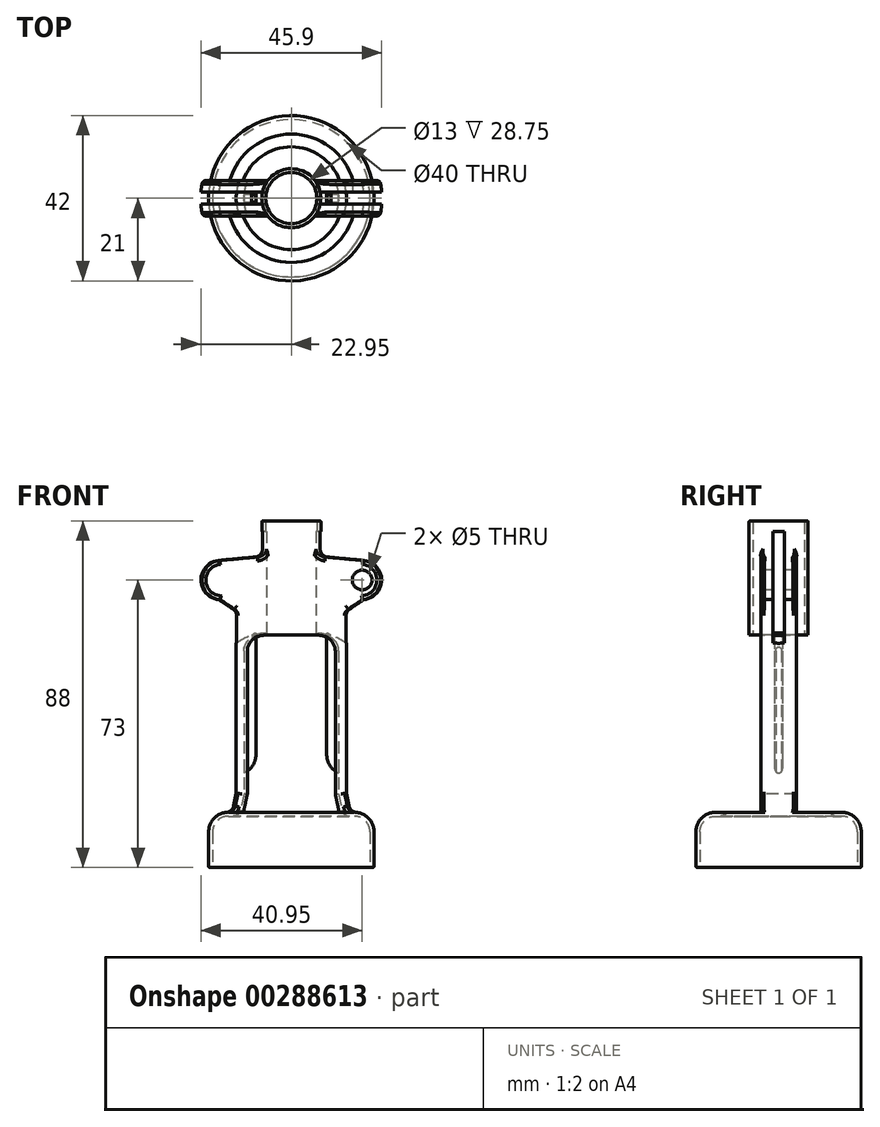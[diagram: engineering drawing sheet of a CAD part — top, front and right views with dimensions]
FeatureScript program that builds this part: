
annotation { "Feature Type Name" : "Feature", "Feature Type Description" : "" }
export const myFeature = defineFeature(function(context is Context, id is Id, definition is map)
    precondition{}
    {
        {
            var Q0;
            Q0=qCreatedBy(makeId("Front.planeOp"),FACE);
            var sketch = newSketch(context, id + "F0", { "sketchPlane" : qUnion([Q0])});
            skLineSegment(sketch, "E0", {"start": v(0, 0) * mm, "end": v(0, 88) * mm, "construction": true});
            skLineSegment(sketch, "E1", {"start": v(0, 88) * mm, "end": v(7.5, 88) * mm, "construction": true});
            skLineSegment(sketch, "E2", {"start": v(0, 79) * mm, "end": v(7.5, 79) * mm, "construction": true});
            skLineSegment(sketch, "E3", {"start": v(0, 73) * mm, "end": v(23, 73) * mm, "construction": true});
            skLineSegment(sketch, "E4", {"start": v(0, 65) * mm, "end": v(14, 65) * mm, "construction": true});
            skLineSegment(sketch, "E5", {"start": v(0, 0) * mm, "end": v(21, 0) * mm, "construction": true});
            skLineSegment(sketch, "E6", {"start": v(21, 0) * mm, "end": v(21, 14) * mm, "construction": true});
            skLineSegment(sketch, "E7", {"start": v(21, 14) * mm, "end": v(0, 14) * mm, "construction": true});
            skLineSegment(sketch, "E8", {"start": v(0, 14) * mm, "end": v(0, 19) * mm, "construction": true});
            skLineSegment(sketch, "E9", {"start": v(0, 19) * mm, "end": v(14, 19) * mm, "construction": true});
            skLineSegment(sketch, "E10", {"start": v(14, 19) * mm, "end": v(15, 14) * mm, "construction": true});
            skLineSegment(sketch, "E11", {"start": v(7.5, 88) * mm, "end": v(7.5, 79) * mm, "construction": true});
            skCircle(sketch, "E12", {"center": v(18, 73) * mm, "radius": 5 * mm, "construction": true});
            skLineSegment(sketch, "E13", {"start": v(7.5, 88) * mm, "end": v(7.5, 79) * mm});
            skLineSegment(sketch, "E14", {"start": v(7.5, 79) * mm, "end": v(18.46, 77.98) * mm});
            skArc(sketch, "E15", {"start": v(18.46, 77.98) * mm, "mid": v(23, 73) * mm, "end": v(18.45, 68.02) * mm});
            skLineSegment(sketch, "E16", {"start": v(18.45, 68.02) * mm, "end": v(14, 65) * mm});
            skLineSegment(sketch, "E17", {"start": v(14, 19) * mm, "end": v(14, 65) * mm});
            skLineSegment(sketch, "E18", {"start": v(14, 19) * mm, "end": v(15, 14) * mm});
            skLineSegment(sketch, "E19", {"start": v(15, 14) * mm, "end": v(16, 14) * mm});
            skLineSegment(sketch, "E20", {"start": v(21, 9) * mm, "end": v(21, 0) * mm});
            skPoint(sketch, "E21.visualSharp", {"position": v(21, 14) * mm});
            skArc(sketch, "E21.filletArc", {"start": v(21, 9) * mm, "mid": v(19.54, 12.54) * mm, "end": v(16, 14) * mm});
            skArc(sketch, "E22.0", {"start": v(20, 9) * mm, "mid": v(18.83, 11.83) * mm, "end": v(16, 13) * mm});
            skLineSegment(sketch, "E23.0", {"start": v(20, 9) * mm, "end": v(20, 0) * mm});
            skLineSegment(sketch, "E24.0", {"start": v(15, 13) * mm, "end": v(16, 13) * mm});
            skLineSegment(sketch, "E25", {"start": v(21, 0) * mm, "end": v(20, 0) * mm});
            skLineSegment(sketch, "E26.0", {"start": v(12.04, 18.6) * mm, "end": v(13.04, 13.6) * mm});
            skLineSegment(sketch, "E27", {"start": v(13.04, 13.6) * mm, "end": v(13.16, 13) * mm});
            skLineSegment(sketch, "E28", {"start": v(15, 13) * mm, "end": v(13.16, 13) * mm});
            skLineSegment(sketch, "E29", {"start": v(7.5, 88) * mm, "end": v(6.5, 88) * mm});
            skLineSegment(sketch, "E30", {"start": v(6.5, 88) * mm, "end": v(6.5, 59) * mm});
            skLineSegment(sketch, "E31", {"start": v(12.04, 18.6) * mm, "end": v(12.04, 55) * mm});
            skLineSegment(sketch, "E32", {"start": v(8.04, 59) * mm, "end": v(6.5, 59) * mm});
            skPoint(sketch, "E33.visualSharp", {"position": v(12.04, 59) * mm});
            skArc(sketch, "E33.filletArc", {"start": v(12.04, 55) * mm, "mid": v(10.87, 57.83) * mm, "end": v(8.04, 59) * mm});
            skSolve(sketch);
        }
        {
            var Q0;
            Q0=makeQuery(id+"F0.imprint","IMPRINT",FACE,{"disambiguationData":[TD([[makeQuery(id+"F0.imprint","IMPRINT",EDGE,{"derivedFrom":sQuery(id+"F0.wireOp",EDGE,"E13")}),-1.0]])]});
            var Q1;
            Q1=sQuery(id+"F0.wireOp",EDGE,"E0");
            revolve(context, id + "F1", {"entities" : qUnion([Q0]), "axis" : qUnion([Q1]), "revolveType" : RevolveType.FULL});
        }
        {
            var Q0;
            Q0=makeQuery(id+"F1.opRevolve","SWEPT_EDGE",EDGE,{"disambiguationData":[OSD([sQuery(id+"F0.wireOp",EDGE,"E13"),sQuery(id+"F0.wireOp",EDGE,"E14")])]});
            var Q1;
            Q1=makeQuery(id+"F1.opRevolve","SWEPT_EDGE",EDGE,{"disambiguationData":[OSD([sQuery(id+"F0.wireOp",EDGE,"E16"),sQuery(id+"F0.wireOp",EDGE,"E17")])]});
            var Q2;
            Q2=makeQuery(id+"F1.opRevolve","SWEPT_EDGE",EDGE,{"disambiguationData":[OSD([sQuery(id+"F0.wireOp",EDGE,"E17"),sQuery(id+"F0.wireOp",EDGE,"E18")])]});
            var Q3;
            Q3=makeQuery(id+"F1.opRevolve","SWEPT_EDGE",EDGE,{"disambiguationData":[OSD([sQuery(id+"F0.wireOp",EDGE,"E18"),sQuery(id+"F0.wireOp",EDGE,"E19")])]});
            fillet(context, id + "F2", {"entities" : qUnion([Q0, Q1, Q2, Q3]), "radius" : 2 * mm, "tangentPropagation" : true, "allowEdgeOverflow" : false});
        }
        {
            var Q0;
            Q0=makeQuery(id+"F1.opRevolve","SWEPT_EDGE",EDGE,{"disambiguationData":[OSD([sQuery(id+"F0.wireOp",EDGE,"E27"),sQuery(id+"F0.wireOp",EDGE,"E28")])]});
            fillet(context, id + "F3", {"entities" : qUnion([Q0]), "radius" : 2 * mm, "tangentPropagation" : true, "allowEdgeOverflow" : false});
        }
        {
            var Q0;
            Q0=makeQuery(id+"F1.opRevolve","SWEPT_FACE",FACE,{"disambiguationData":[OSD([sQuery(id+"F0.wireOp",EDGE,"E29")])]});
            var sketch = newSketch(context, id + "F4", { "sketchPlane" : qUnion([Q0])});
            skCircle(sketch, "E34.0", {"center": v(0, 0) * mm, "radius": 7.5 * mm});
            skCircle(sketch, "E35", {"center": v(0, 0) * mm, "radius": 23 * mm});
            skLineSegment(sketch, "E36", {"start": v(25.66, 0) * mm, "end": v(-26.89, 0) * mm, "construction": true});
            skLineSegment(sketch, "E37", {"start": v(22.56, 4.5) * mm, "end": v(6, 4.5) * mm});
            skLineSegment(sketch, "E38.trimOffspring", {"start": v(-6, 4.5) * mm, "end": v(-22.56, 4.5) * mm});
            skLineSegment(sketch, "E39.MirrorCS", {"start": v(-6, -4.5) * mm, "end": v(-22.56, -4.5) * mm});
            skLineSegment(sketch, "E40.MirrorCS", {"start": v(22.56, -4.5) * mm, "end": v(6, -4.5) * mm});
            skSolve(sketch);
        }
        {
            var Q0;
            {var subQ0=sQuery(id+"F4.wireOp",EDGE,"E37");Q0=makeQuery(id+"F4.imprint","IMPRINT",FACE,{"disambiguationData":[TD([[makeQuery(id+"F4.imprint","IMPRINT",EDGE,{"derivedFrom":subQ0}),-1.0]])]});}
            var Q1;
            {var subQ0=sQuery(id+"F4.wireOp",EDGE,"E39.MirrorCS");Q1=makeQuery(id+"F4.imprint","IMPRINT",FACE,{"disambiguationData":[TD([[makeQuery(id+"F4.imprint","IMPRINT",EDGE,{"derivedFrom":subQ0}),1.0]])]});}
            extrude(context, id + "F5", {"entities" : qUnion([Q0, Q1]), "operationType" : NewBodyOperationType.REMOVE, "oppositeDirection" : true, "depth" : 74 * mm});
        }
        {
            var Q0;
            Q0=qCreatedBy(makeId("Front.planeOp"),FACE);
            var sketch = newSketch(context, id + "F6", { "sketchPlane" : qUnion([Q0])});
            skArc(sketch, "E41", {"start": v(18.45, 68.02) * mm, "mid": v(23, 73) * mm, "end": v(18.46, 77.98) * mm});
            skLineSegment(sketch, "E42", {"start": v(9.31, 78.83) * mm, "end": v(18.46, 77.98) * mm});
            skArc(sketch, "E43", {"start": v(7.5, 80.82) * mm, "mid": v(8.02, 79.48) * mm, "end": v(9.31, 78.83) * mm});
            skLineSegment(sketch, "E44", {"start": v(18.45, 68.02) * mm, "end": v(14.88, 65.6) * mm});
            skArc(sketch, "E45", {"start": v(14.88, 65.6) * mm, "mid": v(14.23, 64.88) * mm, "end": v(14, 63.94) * mm});
            skLineSegment(sketch, "E46", {"start": v(0, 95.54) * mm, "end": v(0, 46.6) * mm, "construction": true});
            skLineSegment(sketch, "E47", {"start": v(7.5, 80.82) * mm, "end": v(7.5, 85.38) * mm});
            skLineSegment(sketch, "E48.MirrorCS", {"start": v(-7.5, 80.82) * mm, "end": v(-7.5, 85.38) * mm});
            skArc(sketch, "E49.MirrorCS", {"start": v(-14.88, 65.6) * mm, "mid": v(-14.23, 64.88) * mm, "end": v(-14, 63.94) * mm});
            skLineSegment(sketch, "E50.MirrorCS", {"start": v(-18.45, 68.02) * mm, "end": v(-14.88, 65.6) * mm});
            skArc(sketch, "E51.MirrorCS", {"start": v(-7.5, 80.82) * mm, "mid": v(-8.02, 79.48) * mm, "end": v(-9.31, 78.83) * mm});
            skLineSegment(sketch, "E52.MirrorCS", {"start": v(-9.31, 78.83) * mm, "end": v(-18.46, 77.98) * mm});
            skArc(sketch, "E53.MirrorCS", {"start": v(-18.45, 68.02) * mm, "mid": v(-23, 73) * mm, "end": v(-18.46, 77.98) * mm});
            skLineSegment(sketch, "E54", {"start": v(7.5, 85.38) * mm, "end": v(-7.5, 85.38) * mm});
            skLineSegment(sketch, "E55", {"start": v(14, 63.94) * mm, "end": v(14, 56.94) * mm});
            skLineSegment(sketch, "E56.0", {"start": v(6, 59) * mm, "end": v(6, 80.82) * mm});
            skLineSegment(sketch, "E57.0", {"start": v(-6, 59) * mm, "end": v(-6, 80.82) * mm});
            skLineSegment(sketch, "E58.0", {"start": v(6, 59) * mm, "end": v(-6, 59) * mm});
            skLineSegment(sketch, "E59", {"start": v(6, 59.5) * mm, "end": v(-6, 59.5) * mm});
            skArc(sketch, "E60", {"start": v(14, 56.94) * mm, "mid": v(10.2, 58.84) * mm, "end": v(6, 59.5) * mm});
            skLineSegment(sketch, "E61.MirrorCS", {"start": v(-6, 59) * mm, "end": v(6, 59) * mm});
            skLineSegment(sketch, "E62.MirrorCS", {"start": v(-14, 63.94) * mm, "end": v(-14, 56.94) * mm});
            skArc(sketch, "E63.MirrorCS", {"start": v(-14, 56.94) * mm, "mid": v(-10.2, 58.84) * mm, "end": v(-6, 59.5) * mm});
            skLineSegment(sketch, "E64.MirrorCS", {"start": v(-7.5, 85.38) * mm, "end": v(7.5, 85.38) * mm});
            skLineSegment(sketch, "E65.MirrorCS", {"start": v(-6, 59.5) * mm, "end": v(6, 59.5) * mm});
            skSolve(sketch);
        }
        {
            var Q0;
            Q0 = qSketchRegion(id + "F6", true);
            extrude(context, id + "F7", {"entities" : qUnion([Q0]), "operationType" : NewBodyOperationType.REMOVE, "endBound" : BoundingType.SYMMETRIC, "oppositeDirection" : true, "depth" : 3 * mm});
        }
        {
            var Q0;
            Q0=qCreatedBy(makeId("Front.planeOp"),FACE);
            var sketch = newSketch(context, id + "F8", { "sketchPlane" : qUnion([Q0])});
            skLineSegment(sketch, "E66.0", {"start": v(11.17, 18.6) * mm, "end": v(11.17, 55) * mm});
            skFitSpline(sketch, "E67.0.0", {"points": [v(13.98, 15.58) * mm, v(13.75, 16.65) * mm, v(13.53, 17.73) * mm, v(13.3, 18.8) * mm]});
            skFitSpline(sketch, "E67.0.1", {"points": [v(13.3, 18.8) * mm, v(13.27, 18.93) * mm, v(13.26, 19.07) * mm, v(13.26, 19.2) * mm]});
            skLineSegment(sketch, "E67.0.2", {"start": v(13.26, 19.2) * mm, "end": v(13.26, 63.94) * mm});
            skFitSpline(sketch, "E67.0.4", {"points": [v(14.18, 65.6) * mm, v(15.42, 66.4) * mm, v(16.66, 67.2) * mm, v(17.9, 68.02) * mm]});
            skFitSpline(sketch, "E67.0.5", {"points": [v(17.9, 68.02) * mm, v(18.2, 68.05) * mm, v(18.82, 68.16) * mm, v(19.55, 68.43) * mm, v(20.1, 68.72) * mm, v(20.5, 68.98) * mm, v(20.86, 69.27) * mm, v(21.2, 69.6) * mm, v(21.5, 69.95) * mm, v(21.78, 70.33) * mm, v(22.01, 70.74) * mm, v(22.2, 71.17) * mm, v(22.36, 71.6) * mm, v(22.47, 72.06) * mm, v(22.54, 72.53) * mm, v(22.57, 73.16) * mm, v(22.51, 73.77) * mm, v(22.36, 74.38) * mm, v(22.21, 74.83) * mm, v(22.02, 75.25) * mm, v(21.79, 75.66) * mm, v(21.51, 76.04) * mm, v(21.2, 76.4) * mm, v(20.87, 76.72) * mm, v(20.5, 77.01) * mm, v(20.11, 77.27) * mm, v(19.7, 77.5) * mm, v(19.28, 77.67) * mm, v(18.83, 77.82) * mm, v(18.37, 77.92) * mm, v(18.06, 77.96) * mm, v(17.9, 77.98) * mm]});
            skFitSpline(sketch, "E67.0.6", {"points": [v(17.9, 77.98) * mm, v(16.28, 78.13) * mm, v(13.03, 78.42) * mm, v(9.78, 78.7) * mm, v(8.16, 78.83) * mm]});
            skLineSegment(sketch, "E67.0.8", {"start": v(6, 80.82) * mm, "end": v(6, 59) * mm});
            skFitSpline(sketch, "E67.0.12", {"points": [v(11.17, 18.6) * mm, v(11.45, 17.27) * mm, v(11.74, 15.94) * mm, v(12.02, 14.6) * mm]});
            skLineSegment(sketch, "E67.0.14", {"start": v(12.27, 14) * mm, "end": v(15.67, 14) * mm});
            skFitSpline(sketch, "E68.0.0", {"points": [v(13.98, 15.58) * mm, v(13.75, 16.65) * mm, v(13.53, 17.73) * mm, v(13.3, 18.8) * mm]});
            skFitSpline(sketch, "E68.0.1", {"points": [v(13.3, 18.8) * mm, v(13.27, 18.93) * mm, v(13.26, 19.07) * mm, v(13.26, 19.2) * mm]});
            skFitSpline(sketch, "E68.0.4", {"points": [v(14.18, 65.6) * mm, v(15.42, 66.4) * mm, v(16.66, 67.2) * mm, v(17.9, 68.02) * mm]});
            skFitSpline(sketch, "E68.0.5", {"points": [v(17.9, 68.02) * mm, v(18.2, 68.05) * mm, v(18.82, 68.16) * mm, v(19.55, 68.43) * mm, v(20.1, 68.72) * mm, v(20.5, 68.98) * mm, v(20.86, 69.27) * mm, v(21.2, 69.6) * mm, v(21.5, 69.95) * mm, v(21.78, 70.33) * mm, v(22.01, 70.74) * mm, v(22.2, 71.17) * mm, v(22.36, 71.6) * mm, v(22.47, 72.06) * mm, v(22.54, 72.53) * mm, v(22.57, 73.16) * mm, v(22.51, 73.77) * mm, v(22.36, 74.38) * mm, v(22.21, 74.83) * mm, v(22.02, 75.25) * mm, v(21.79, 75.66) * mm, v(21.51, 76.04) * mm, v(21.2, 76.4) * mm, v(20.87, 76.72) * mm, v(20.5, 77.01) * mm, v(20.11, 77.27) * mm, v(19.7, 77.5) * mm, v(19.28, 77.67) * mm, v(18.83, 77.82) * mm, v(18.37, 77.92) * mm, v(18.06, 77.96) * mm, v(17.9, 77.98) * mm]});
            skFitSpline(sketch, "E68.0.6", {"points": [v(17.9, 77.98) * mm, v(16.28, 78.13) * mm, v(13.03, 78.42) * mm, v(9.78, 78.7) * mm, v(8.16, 78.83) * mm]});
            skLineSegment(sketch, "E68.0.9", {"start": v(6, 59) * mm, "end": v(6.66, 59) * mm});
            skFitSpline(sketch, "E68.0.12", {"points": [v(11.17, 18.6) * mm, v(11.45, 17.27) * mm, v(11.74, 15.94) * mm, v(12.02, 14.6) * mm]});
            skLineSegment(sketch, "E69.0", {"start": v(12.02, 18.6) * mm, "end": v(12.02, 55) * mm});
            skPoint(sketch, "E70", {"position": v(6.66, 59.85) * mm});
            skArc(sketch, "E71", {"start": v(12.02, 55) * mm, "mid": v(10.41, 58.61) * mm, "end": v(6.66, 59.85) * mm});
            skLineSegment(sketch, "E72", {"start": v(9, 59.5) * mm, "end": v(9, 28.59) * mm});
            skArc(sketch, "E73", {"start": v(9, 28.59) * mm, "mid": v(9.82, 25.84) * mm, "end": v(12.02, 24) * mm});
            skLineSegment(sketch, "E74", {"start": v(0, 88.09) * mm, "end": v(0, 116.69) * mm, "construction": true});
            skLineSegment(sketch, "E75.MirrorCS", {"start": v(-9, 59.5) * mm, "end": v(-9, 28.59) * mm});
            skArc(sketch, "E76.MirrorCS", {"start": v(-12.02, 55) * mm, "mid": v(-10.41, 58.61) * mm, "end": v(-6.66, 59.85) * mm});
            skLineSegment(sketch, "E77.MirrorCS", {"start": v(-12.02, 18.6) * mm, "end": v(-12.02, 55) * mm});
            skArc(sketch, "E78.MirrorCS", {"start": v(-9, 28.59) * mm, "mid": v(-9.82, 25.84) * mm, "end": v(-12.02, 24) * mm});
            skSolve(sketch);
        }
        {
            var Q0;
            {var subQ0=sQuery(id+"F8.wireOp",EDGE,"E75.MirrorCS");Q0=makeQuery(id+"F8.imprint","IMPRINT",FACE,{"disambiguationData":[TD([[makeQuery(id+"F8.imprint","IMPRINT",EDGE,{"derivedFrom":subQ0}),-1.0]])]});}
            var Q1;
            {var subQ5=sQuery(id+"F8.wireOp",EDGE,"E72");Q1=makeQuery(id+"F8.imprint","IMPRINT",FACE,{"disambiguationData":[TD([[makeQuery(id+"F8.imprint","IMPRINT",EDGE,{"derivedFrom":subQ5}),1.0]])]});}
            extrude(context, id + "F9", {"entities" : qUnion([Q0, Q1]), "operationType" : NewBodyOperationType.ADD, "endBound" : BoundingType.SYMMETRIC, "depth" : 2 * mm});
        }
        {
            var Q0;
            Q0=makeQuery(id+"F5.boolean.opBoolean","COPY",FACE,{"derivedFrom":makeQuery(id+"F5.opExtrude","SWEPT_FACE",FACE,{"disambiguationData":[OSD([sQuery(id+"F4.wireOp",EDGE,"E40.MirrorCS")])]})});
            var sketch = newSketch(context, id + "F10", { "sketchPlane" : qUnion([Q0])});
            skCircle(sketch, "E79", {"center": v(18, 73) * mm, "radius": 2.5 * mm});
            skFitSpline(sketch, "E80.0", {"points": [v(12.99, 70.36) * mm, v(12.73, 70.79) * mm, v(12.53, 71.25) * mm, v(12.37, 71.72) * mm, v(12.26, 72.2) * mm, v(12.18, 72.87) * mm, v(12.2, 73.53) * mm, v(12.34, 74.2) * mm, v(12.5, 74.67) * mm, v(12.7, 75.13) * mm, v(13.02, 75.71) * mm, v(13.53, 76.37) * mm, v(14.17, 76.92) * mm, v(14.73, 77.28) * mm, v(15.17, 77.5) * mm, v(15.64, 77.7) * mm, v(16.11, 77.84) * mm, v(16.6, 77.94) * mm, v(17.1, 78) * mm, v(17.6, 78) * mm, v(18.1, 77.97) * mm, v(18.59, 77.88) * mm, v(19.23, 77.7) * mm, v(20, 77.37) * mm, v(20.82, 76.8) * mm, v(21.4, 76.2) * mm, v(21.79, 75.65) * mm, v(22.04, 75.22) * mm, v(22.24, 74.76) * mm, v(22.4, 74.29) * mm, v(22.5, 73.8) * mm, v(22.55, 73.3) * mm, v(22.56, 72.8) * mm, v(22.5, 72.13) * mm, v(22.34, 71.5) * mm, v(22.08, 70.87) * mm, v(21.84, 70.43) * mm, v(21.56, 70.02) * mm, v(21.24, 69.63) * mm, v(20.88, 69.28) * mm, v(20.49, 68.97) * mm, v(20.07, 68.7) * mm, v(19.47, 68.4) * mm, v(18.85, 68.17) * mm, v(18.19, 68.05) * mm, v(17.7, 68) * mm, v(17.2, 68) * mm, v(16.7, 68.04) * mm, v(16.2, 68.13) * mm, v(15.72, 68.27) * mm, v(15.26, 68.45) * mm, v(14.8, 68.67) * mm, v(14.38, 68.94) * mm, v(13.99, 69.24) * mm, v(13.62, 69.58) * mm, v(13.28, 69.95) * mm, v(12.99, 70.36) * mm, v(12.73, 70.79) * mm, v(12.53, 71.25) * mm]});
            skLineSegment(sketch, "E81", {"start": v(0, 88.18) * mm, "end": v(0, 40.08) * mm, "construction": true});
            skCircle(sketch, "E82.MirrorC", {"center": v(-18, 73) * mm, "radius": 2.5 * mm});
            skSolve(sketch);
        }
        {
            var Q0;
            Q0=makeQuery(id+"F10.imprint","IMPRINT",FACE,{"disambiguationData":[TD([[makeQuery(id+"F10.imprint","IMPRINT",EDGE,{"derivedFrom":sQuery(id+"F10.wireOp",EDGE,"E79")}),1.0]])]});
            var Q1;
            Q1=makeQuery(id+"F10.imprint","IMPRINT",FACE,{"disambiguationData":[TD([[makeQuery(id+"F10.imprint","IMPRINT",EDGE,{"derivedFrom":sQuery(id+"F10.wireOp",EDGE,"E82.MirrorC")}),-1.0]])]});
            extrude(context, id + "F11", {"entities" : qUnion([Q0, Q1]), "operationType" : NewBodyOperationType.REMOVE, "endBound" : BoundingType.THROUGH_ALL, "oppositeDirection" : true, "depth" : 24.4 * mm});
        }
        {
            var Q0;
            Q0=makeQuery(id+"F5.boolean.opBoolean","INTERSECT",EDGE,{"derivedFrom":[makeQuery(id+"F2.opFillet","BLEND_FACE",FACE,{"disambiguationData":[OSD([sQuery(id+"F0.wireOp",EDGE,"E13"),sQuery(id+"F0.wireOp",EDGE,"E14")])]}),makeQuery(id+"F5.opExtrude","SWEPT_FACE",FACE,{"disambiguationData":[OSD([sQuery(id+"F4.wireOp",EDGE,"E39.MirrorCS")])]})]});
            var Q1;
            Q1=makeQuery(id+"F5.boolean.opBoolean","INTERSECT",EDGE,{"derivedFrom":[makeQuery(id+"F1.opRevolve","SWEPT_FACE",FACE,{"disambiguationData":[OSD([sQuery(id+"F0.wireOp",EDGE,"E14")])]}),makeQuery(id+"F5.opExtrude","SWEPT_FACE",FACE,{"disambiguationData":[OSD([sQuery(id+"F4.wireOp",EDGE,"E39.MirrorCS")])]})]});
            var Q2;
            Q2=makeQuery(id+"F5.boolean.opBoolean","INTERSECT",EDGE,{"derivedFrom":[makeQuery(id+"F1.opRevolve","SWEPT_FACE",FACE,{"disambiguationData":[OSD([sQuery(id+"F0.wireOp",EDGE,"E15")])]}),makeQuery(id+"F5.opExtrude","SWEPT_FACE",FACE,{"disambiguationData":[OSD([sQuery(id+"F4.wireOp",EDGE,"E39.MirrorCS")])]})]});
            var Q3;
            Q3=makeQuery(id+"F5.boolean.opBoolean","INTERSECT",EDGE,{"derivedFrom":[makeQuery(id+"F1.opRevolve","SWEPT_FACE",FACE,{"disambiguationData":[OSD([sQuery(id+"F0.wireOp",EDGE,"E16")])]}),makeQuery(id+"F5.opExtrude","SWEPT_FACE",FACE,{"disambiguationData":[OSD([sQuery(id+"F4.wireOp",EDGE,"E39.MirrorCS")])]})]});
            var Q4;
            Q4=makeQuery(id+"F5.boolean.opBoolean","INTERSECT",EDGE,{"derivedFrom":[makeQuery(id+"F2.opFillet","BLEND_FACE",FACE,{"disambiguationData":[OSD([sQuery(id+"F0.wireOp",EDGE,"E16"),sQuery(id+"F0.wireOp",EDGE,"E17")])]}),makeQuery(id+"F5.opExtrude","SWEPT_FACE",FACE,{"disambiguationData":[OSD([sQuery(id+"F4.wireOp",EDGE,"E39.MirrorCS")])]})]});
            var Q5;
            Q5=makeQuery(id+"F5.boolean.opBoolean","INTERSECT",EDGE,{"derivedFrom":[makeQuery(id+"F2.opFillet","BLEND_FACE",FACE,{"disambiguationData":[OSD([sQuery(id+"F0.wireOp",EDGE,"E13"),sQuery(id+"F0.wireOp",EDGE,"E14")])]}),makeQuery(id+"F5.opExtrude","SWEPT_FACE",FACE,{"disambiguationData":[OSD([sQuery(id+"F4.wireOp",EDGE,"E40.MirrorCS")])]})]});
            var Q6;
            Q6=makeQuery(id+"F5.boolean.opBoolean","INTERSECT",EDGE,{"derivedFrom":[makeQuery(id+"F1.opRevolve","SWEPT_FACE",FACE,{"disambiguationData":[OSD([sQuery(id+"F0.wireOp",EDGE,"E14")])]}),makeQuery(id+"F5.opExtrude","SWEPT_FACE",FACE,{"disambiguationData":[OSD([sQuery(id+"F4.wireOp",EDGE,"E40.MirrorCS")])]})]});
            var Q7;
            Q7=makeQuery(id+"F5.boolean.opBoolean","INTERSECT",EDGE,{"derivedFrom":[makeQuery(id+"F1.opRevolve","SWEPT_FACE",FACE,{"disambiguationData":[OSD([sQuery(id+"F0.wireOp",EDGE,"E16")])]}),makeQuery(id+"F5.opExtrude","SWEPT_FACE",FACE,{"disambiguationData":[OSD([sQuery(id+"F4.wireOp",EDGE,"E40.MirrorCS")])]})]});
            var Q8;
            Q8=makeQuery(id+"F5.boolean.opBoolean","INTERSECT",EDGE,{"derivedFrom":[makeQuery(id+"F2.opFillet","BLEND_FACE",FACE,{"disambiguationData":[OSD([sQuery(id+"F0.wireOp",EDGE,"E16"),sQuery(id+"F0.wireOp",EDGE,"E17")])]}),makeQuery(id+"F5.opExtrude","SWEPT_FACE",FACE,{"disambiguationData":[OSD([sQuery(id+"F4.wireOp",EDGE,"E40.MirrorCS")])]})]});
            var Q9;
            Q9=makeQuery(id+"F5.boolean.opBoolean","INTERSECT",EDGE,{"derivedFrom":[makeQuery(id+"F2.opFillet","BLEND_FACE",FACE,{"disambiguationData":[OSD([sQuery(id+"F0.wireOp",EDGE,"E13"),sQuery(id+"F0.wireOp",EDGE,"E14")])]}),makeQuery(id+"F5.opExtrude","SWEPT_FACE",FACE,{"disambiguationData":[OSD([sQuery(id+"F4.wireOp",EDGE,"E37")])]})]});
            var Q10;
            Q10=makeQuery(id+"F5.boolean.opBoolean","INTERSECT",EDGE,{"derivedFrom":[makeQuery(id+"F1.opRevolve","SWEPT_FACE",FACE,{"disambiguationData":[OSD([sQuery(id+"F0.wireOp",EDGE,"E14")])]}),makeQuery(id+"F5.opExtrude","SWEPT_FACE",FACE,{"disambiguationData":[OSD([sQuery(id+"F4.wireOp",EDGE,"E37")])]})]});
            var Q11;
            Q11=makeQuery(id+"F5.boolean.opBoolean","INTERSECT",EDGE,{"derivedFrom":[makeQuery(id+"F1.opRevolve","SWEPT_FACE",FACE,{"disambiguationData":[OSD([sQuery(id+"F0.wireOp",EDGE,"E15")])]}),makeQuery(id+"F5.opExtrude","SWEPT_FACE",FACE,{"disambiguationData":[OSD([sQuery(id+"F4.wireOp",EDGE,"E37")])]})]});
            var Q12;
            Q12=makeQuery(id+"F5.boolean.opBoolean","INTERSECT",EDGE,{"derivedFrom":[makeQuery(id+"F1.opRevolve","SWEPT_FACE",FACE,{"disambiguationData":[OSD([sQuery(id+"F0.wireOp",EDGE,"E16")])]}),makeQuery(id+"F5.opExtrude","SWEPT_FACE",FACE,{"disambiguationData":[OSD([sQuery(id+"F4.wireOp",EDGE,"E37")])]})]});
            var Q13;
            Q13=makeQuery(id+"F5.boolean.opBoolean","INTERSECT",EDGE,{"derivedFrom":[makeQuery(id+"F2.opFillet","BLEND_FACE",FACE,{"disambiguationData":[OSD([sQuery(id+"F0.wireOp",EDGE,"E13"),sQuery(id+"F0.wireOp",EDGE,"E14")])]}),makeQuery(id+"F5.opExtrude","SWEPT_FACE",FACE,{"disambiguationData":[OSD([sQuery(id+"F4.wireOp",EDGE,"E38.trimOffspring")])]})]});
            var Q14;
            Q14=makeQuery(id+"F5.boolean.opBoolean","INTERSECT",EDGE,{"derivedFrom":[makeQuery(id+"F1.opRevolve","SWEPT_FACE",FACE,{"disambiguationData":[OSD([sQuery(id+"F0.wireOp",EDGE,"E14")])]}),makeQuery(id+"F5.opExtrude","SWEPT_FACE",FACE,{"disambiguationData":[OSD([sQuery(id+"F4.wireOp",EDGE,"E38.trimOffspring")])]})]});
            var Q15;
            Q15=makeQuery(id+"F5.boolean.opBoolean","INTERSECT",EDGE,{"derivedFrom":[makeQuery(id+"F1.opRevolve","SWEPT_FACE",FACE,{"disambiguationData":[OSD([sQuery(id+"F0.wireOp",EDGE,"E15")])]}),makeQuery(id+"F5.opExtrude","SWEPT_FACE",FACE,{"disambiguationData":[OSD([sQuery(id+"F4.wireOp",EDGE,"E38.trimOffspring")])]})]});
            var Q16;
            Q16=makeQuery(id+"F5.boolean.opBoolean","INTERSECT",EDGE,{"derivedFrom":[makeQuery(id+"F1.opRevolve","SWEPT_FACE",FACE,{"disambiguationData":[OSD([sQuery(id+"F0.wireOp",EDGE,"E16")])]}),makeQuery(id+"F5.opExtrude","SWEPT_FACE",FACE,{"disambiguationData":[OSD([sQuery(id+"F4.wireOp",EDGE,"E38.trimOffspring")])]})]});
            fillet(context, id + "F12", {"entities" : qUnion([Q0, Q1, Q2, Q3, Q4, Q5, Q6, Q7, Q8, Q9, Q10, Q11, Q12, Q13, Q14, Q15, Q16]), "radius" : 1 * mm, "tangentPropagation" : true, "allowEdgeOverflow" : false});
        }
        {
            var Q0;
            Q0=makeQuery(id+"F1.opRevolve","SWEPT_EDGE",EDGE,{"disambiguationData":[OSD([sQuery(id+"F0.wireOp",EDGE,"E20"),sQuery(id+"F0.wireOp",EDGE,"E25")])]});
            var Q1;
            Q1=makeQuery(id+"F1.opRevolve","SWEPT_EDGE",EDGE,{"disambiguationData":[OSD([sQuery(id+"F0.wireOp",EDGE,"E23.0"),sQuery(id+"F0.wireOp",EDGE,"E25")])]});
            fillet(context, id + "F13", {"entities" : qUnion([Q0, Q1]), "radius" : .25 * mm, "tangentPropagation" : true, "allowEdgeOverflow" : false});
        }
        {
            var Q0;
            Q0=makeQuery(id+"F11.boolean.opBoolean","COPY",EDGE,{"derivedFrom":makeQuery(id+"F11.opExtrude","CAP_EDGE",EDGE,{"disambiguationData":[OSD([sQuery(id+"F10.wireOp",EDGE,"E79")])],"isStart":true})});
            var Q1;
            Q1=makeQuery(id+"F11.boolean.opBoolean","COPY",EDGE,{"derivedFrom":makeQuery(id+"F11.opExtrude","CAP_EDGE",EDGE,{"disambiguationData":[OSD([sQuery(id+"F10.wireOp",EDGE,"E82.MirrorC")])],"isStart":true})});
            var Q2;
            Q2=makeQuery(id+"F5.boolean.opBoolean","COPY",EDGE,{"derivedFrom":makeQuery(id+"F5.opExtrude","SWEPT_EDGE",EDGE,{"disambiguationData":[OSD([sQuery(id+"F4.wireOp",EDGE,"E34.0"),sQuery(id+"F4.wireOp",EDGE,"E39.MirrorCS")])]})});
            var Q3;
            Q3=makeQuery(id+"F5.boolean.opBoolean","COPY",EDGE,{"derivedFrom":makeQuery(id+"F5.opExtrude","SWEPT_EDGE",EDGE,{"disambiguationData":[OSD([sQuery(id+"F4.wireOp",EDGE,"E34.0"),sQuery(id+"F4.wireOp",EDGE,"E40.MirrorCS")])]})});
            var Q4;
            Q4=makeQuery(id+"F11.boolean.opBoolean","INTERSECT",EDGE,{"derivedFrom":[makeQuery(id+"F5.boolean.opBoolean","COPY",FACE,{"derivedFrom":makeQuery(id+"F5.opExtrude","SWEPT_FACE",FACE,{"disambiguationData":[OSD([sQuery(id+"F4.wireOp",EDGE,"E37")])]})}),makeQuery(id+"F11.opExtrude","SWEPT_FACE",FACE,{"disambiguationData":[OSD([sQuery(id+"F10.wireOp",EDGE,"E79")])]})]});
            var Q5;
            Q5=makeQuery(id+"F11.boolean.opBoolean","INTERSECT",EDGE,{"derivedFrom":[makeQuery(id+"F5.boolean.opBoolean","COPY",FACE,{"derivedFrom":makeQuery(id+"F5.opExtrude","SWEPT_FACE",FACE,{"disambiguationData":[OSD([sQuery(id+"F4.wireOp",EDGE,"E38.trimOffspring")])]})}),makeQuery(id+"F11.opExtrude","SWEPT_FACE",FACE,{"disambiguationData":[OSD([sQuery(id+"F10.wireOp",EDGE,"E82.MirrorC")])]})]});
            var Q6;
            Q6=makeQuery(id+"F5.boolean.opBoolean","COPY",EDGE,{"derivedFrom":makeQuery(id+"F5.opExtrude","SWEPT_EDGE",EDGE,{"disambiguationData":[OSD([sQuery(id+"F4.wireOp",EDGE,"E34.0"),sQuery(id+"F4.wireOp",EDGE,"E38.trimOffspring")])]})});
            var Q7;
            Q7=makeQuery(id+"F5.boolean.opBoolean","COPY",EDGE,{"derivedFrom":makeQuery(id+"F5.opExtrude","SWEPT_EDGE",EDGE,{"disambiguationData":[OSD([sQuery(id+"F4.wireOp",EDGE,"E34.0"),sQuery(id+"F4.wireOp",EDGE,"E37")])]})});
            fillet(context, id + "F14", {"entities" : qUnion([Q0, Q1, Q2, Q3, Q4, Q5, Q6, Q7]), "radius" : .25 * mm, "tangentPropagation" : true, "allowEdgeOverflow" : false});
        }
        {
            var Q0;
            Q0=makeQuery(id+"F1.opRevolve","SWEPT_EDGE",EDGE,{"disambiguationData":[OSD([sQuery(id+"F0.wireOp",EDGE,"E13"),sQuery(id+"F0.wireOp",EDGE,"E29")])]});
            var Q1;
            Q1=makeQuery(id+"F1.opRevolve","SWEPT_EDGE",EDGE,{"disambiguationData":[OSD([sQuery(id+"F0.wireOp",EDGE,"E29"),sQuery(id+"F0.wireOp",EDGE,"E30")])]});
            fillet(context, id + "F15", {"entities" : qUnion([Q0, Q1]), "radius" : .25 * mm, "tangentPropagation" : true, "allowEdgeOverflow" : false});
        }
        {
            var Q0;
            {var subQ1=sQuery(id+"F8.wireOp",EDGE,"E72");Q0=makeQuery(id+"F9.boolean.opBoolean","SPLIT",EDGE,{"disambiguationData":[TD([makeQuery(id+"F1.opRevolve","SWEPT_FACE",FACE,{"disambiguationData":[OSD([sQuery(id+"F0.wireOp",EDGE,"E33.filletArc")])]})])],"derivedFrom":makeQuery(id+"F9.opExtrude","CAP_EDGE",EDGE,{"disambiguationData":[OSD([subQ1])],"isStart":false})});}
            var Q1;
            Q1=makeQuery(id+"F9.opExtrude","CAP_EDGE",EDGE,{"disambiguationData":[OSD([sQuery(id+"F8.wireOp",EDGE,"E73")])],"isStart":false});
            var Q2;
            Q2=makeQuery(id+"F9.opExtrude","CAP_EDGE",EDGE,{"disambiguationData":[OSD([sQuery(id+"F8.wireOp",EDGE,"E78.MirrorCS")])],"isStart":false});
            var Q3;
            Q3=makeQuery(id+"F9.opExtrude","CAP_EDGE",EDGE,{"disambiguationData":[OSD([sQuery(id+"F8.wireOp",EDGE,"E73")])],"isStart":true});
            var Q4;
            Q4=makeQuery(id+"F9.opExtrude","CAP_EDGE",EDGE,{"disambiguationData":[OSD([sQuery(id+"F8.wireOp",EDGE,"E78.MirrorCS")])],"isStart":true});
            fillet(context, id + "F16", {"entities" : qUnion([Q0, Q1, Q2, Q3, Q4]), "radius" : 1 * mm, "tangentPropagation" : true, "allowEdgeOverflow" : false});
        }
    });
